# Revit family: ESC 3 EMERGENCY EXIT LIGHT TW49422
name_source: partatom
category: Electrical Fixtures
revit_build: Autodesk Revit 2015 (Build: 20160512_0715(x64)
units: mm (PartAtom-declared; Revit-internal decimal feet)

## types (3) — shared parameters
Depth = 121 mm  [stored 0.396982 ft]
Height = 634 mm  [stored 2.08005 ft]
Manufacturer = Teknoware Oy
Model = ESC 3
Product Code = TW49422
Viewing Distance = 120000 mm
Width = 1259 mm  [stored 4.13058 ft]

## per-type parameters (varying)
| type | Back Pictogram | Down | Front Pictogram | Left | Right | Type Comments |
| -arrow right | Teknoware Pictogram PB4941E | No | Teknoware Pictogram PB4942E | No | Yes | PB4942E |
| -arrow left | Teknoware Pictogram PB4942E | No | Teknoware Pictogram PB4941E | Yes | No | PB4941E |
| -arrow down | Teknoware Pictogram PB4943E | Yes | Teknoware Pictogram PB4943E | No | No | PB4943E |

note: [stored X ft] marks values corroborated as IEEE doubles in the binary element streams (Revit-internal decimal feet)

## geometry (parser evidence)
native form markers: Blend x12, Sweep x12
no freeform markers — native parametric forms only
